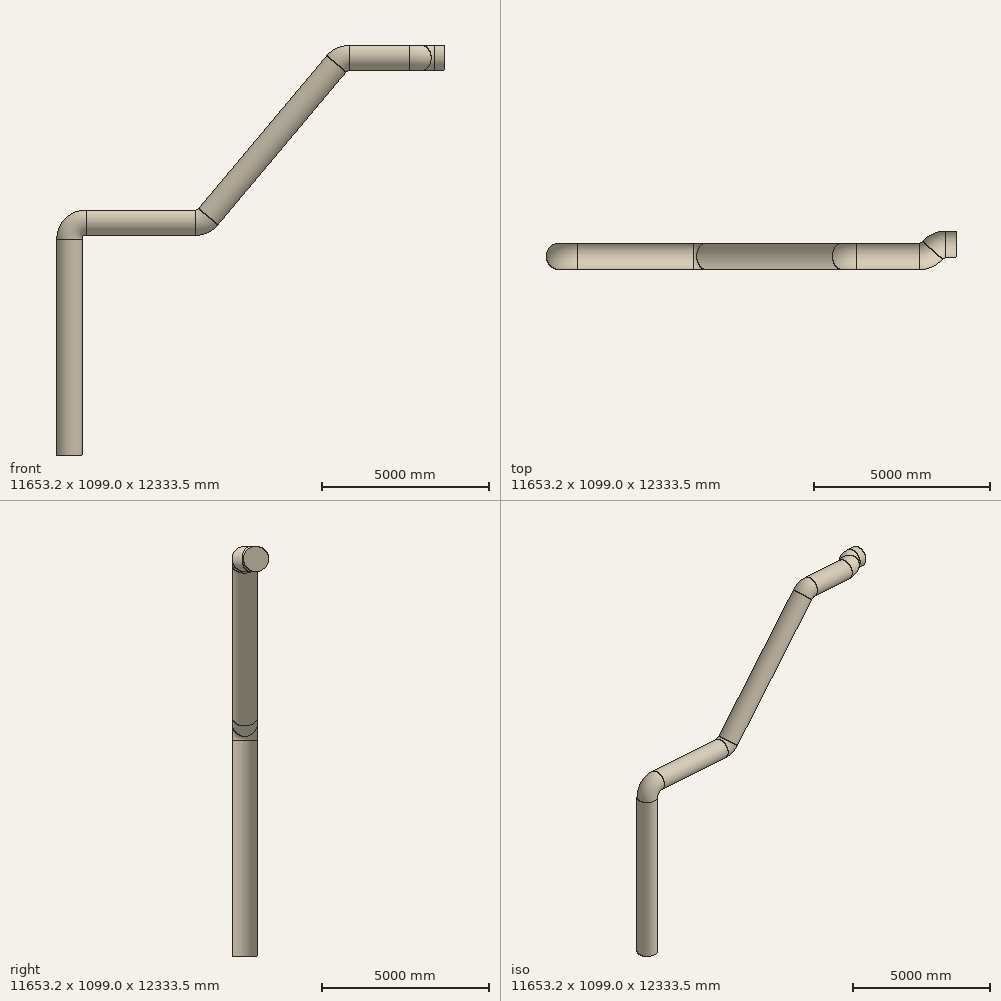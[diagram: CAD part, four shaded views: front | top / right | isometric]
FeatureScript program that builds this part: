
annotation { "Feature Type Name" : "Feature", "Feature Type Description" : "" }
export const myFeature = defineFeature(function(context is Context, id is Id, definition is map)
    precondition{}
    {
        {
            var Q0;
            Q0=qCreatedBy(makeId("Front.planeOp"),FACE);
            var sketch = newSketch(context, id + "F0", { "sketchPlane" : qUnion([Q0])});
            skLineSegment(sketch, "E0", {"start": v(0, 0) * mm, "end": v(0, 6500) * mm});
            skArc(sketch, "E1", {"start": v(500, 7000) * mm, "mid": v(146.45, 6853.55) * mm, "end": v(0, 6500) * mm});
            skLineSegment(sketch, "E2", {"start": v(500, 7000) * mm, "end": v(3800, 7000) * mm});
            skArc(sketch, "E3", {"start": v(3800, 7000) * mm, "mid": v(4011.3, 7046.85) * mm, "end": v(4183.02, 7178.6) * mm});
            skLineSegment(sketch, "E4", {"start": v(4183.02, 7178.6) * mm, "end": v(8039.75, 11774.87) * mm});
            skArc(sketch, "E5", {"start": v(8422.77, 11953.48) * mm, "mid": v(8211.46, 11906.63) * mm, "end": v(8039.75, 11774.87) * mm});
            skLineSegment(sketch, "E6", {"start": v(8422.77, 11953.48) * mm, "end": v(10222.77, 11953.48) * mm});
            skSolve(sketch);
        }
        {
            var Q0;
            Q0=qCreatedBy(makeId("Top.planeOp"),FACE);
            var sketch = newSketch(context, id + "F1", { "sketchPlane" : qUnion([Q0])});
            skCircle(sketch, "E7", {"center": v(0, 0) * mm, "radius": 380 * mm});
            skSolve(sketch);
        }
        {
            var Q0;
            Q0=sQuery(id+"F0.wireOp",VERTEX,"E6.end");
            var Q1;
            Q1=qCreatedBy(makeId("Top.planeOp"),FACE);
            cPlane(context, id + "F2", {"entities" : qUnion([Q0, Q1]), "cplaneType" : CPlaneType.PLANE_POINT, "offset" : 25 * mm, "width" : 150 * mm, "height" : 150 * mm});
        }
        {
            var Q0;
            Q0=qCreatedBy(id+"F2.planeOp",FACE);
            var sketch = newSketch(context, id + "F3", { "sketchPlane" : qUnion([Q0])});
            skArc(sketch, "E8", {"start": v(10222.77, 0) * mm, "mid": v(10428.63, 44.35) * mm, "end": v(10597.98, 169.52) * mm});
            skArc(sketch, "E9", {"start": v(10973.2, 339.04) * mm, "mid": v(10767.33, 294.7) * mm, "end": v(10597.98, 169.52) * mm});
            skLineSegment(sketch, "E10", {"start": v(10973.2, 339.04) * mm, "end": v(11273.2, 339.04) * mm});
            skLineSegment(sketch, "E11", {"start": v(10369.23, 169.52) * mm, "end": v(11010.87, 169.52) * mm, "construction": true});
            skSolve(sketch);
        }
        {
            var Q0;
            Q0=makeQuery(id+"F1.imprint","IMPRINT",FACE,{"disambiguationData":[TD([[makeQuery(id+"F1.imprint","IMPRINT",EDGE,{"derivedFrom":sQuery(id+"F1.wireOp",EDGE,"E7")}),1.0]])]});
            var Q1;
            Q1=sQuery(id+"F0.wireOp",EDGE,"E0");
            var Q2;
            Q2=sQuery(id+"F0.wireOp",EDGE,"E1");
            var Q3;
            Q3=sQuery(id+"F0.wireOp",EDGE,"E2");
            var Q4;
            Q4=sQuery(id+"F0.wireOp",EDGE,"E3");
            var Q5;
            Q5=sQuery(id+"F0.wireOp",EDGE,"E4");
            var Q6;
            Q6=sQuery(id+"F0.wireOp",EDGE,"E5");
            var Q7;
            Q7=sQuery(id+"F0.wireOp",EDGE,"E6");
            var Q8;
            Q8=sQuery(id+"F3.wireOp",EDGE,"E8");
            var Q9;
            Q9=sQuery(id+"F3.wireOp",EDGE,"E9");
            var Q10;
            Q10=sQuery(id+"F3.wireOp",EDGE,"E10");
            sweep(context, id + "F4", {"profiles" : qUnion([Q0]), "path" : qUnion([Q1, Q2, Q3, Q4, Q5, Q6, Q7, Q8, Q9, Q10])});
        }
    });
